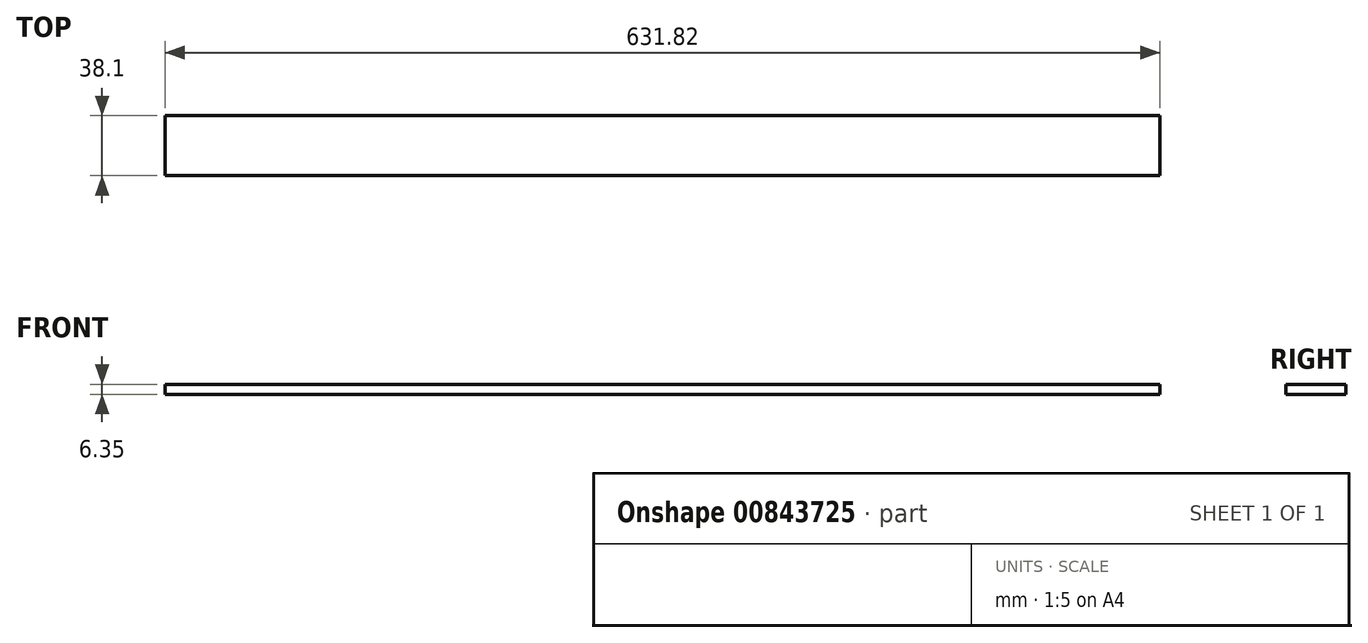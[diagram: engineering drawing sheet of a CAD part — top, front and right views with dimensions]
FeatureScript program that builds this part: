
annotation { "Feature Type Name" : "Feature", "Feature Type Description" : "" }
export const myFeature = defineFeature(function(context is Context, id is Id, definition is map)
    precondition{}
    {
        {
            var Q0;
            Q0=qCreatedBy(makeId("Top.planeOp"),FACE);
            var sketch = newSketch(context, id + "F0", { "sketchPlane" : qUnion([Q0])});
            skLineSegment(sketch, "E0.bottom", {"start": v(315.91, 19.05) * mm, "end": v(-315.91, 19.05) * mm});
            skLineSegment(sketch, "E0.top", {"start": v(315.91, -19.05) * mm, "end": v(-315.91, -19.05) * mm});
            skLineSegment(sketch, "E0.left", {"start": v(315.91, 19.05) * mm, "end": v(315.91, -19.05) * mm});
            skLineSegment(sketch, "E0.right", {"start": v(-315.91, 19.05) * mm, "end": v(-315.91, -19.05) * mm});
            skPoint(sketch, "E0.middle", {"position": v(0, 0) * mm});
            skSolve(sketch);
        }
        {
            var Q0;
            Q0=qSketchRegion(id+"F0",true);
            extrude(context, id + "F1", {"entities" : qUnion([Q0]), "depth" : 6.35 * mm, "offsetDistance" : 25.4 * mm});
        }
    });
